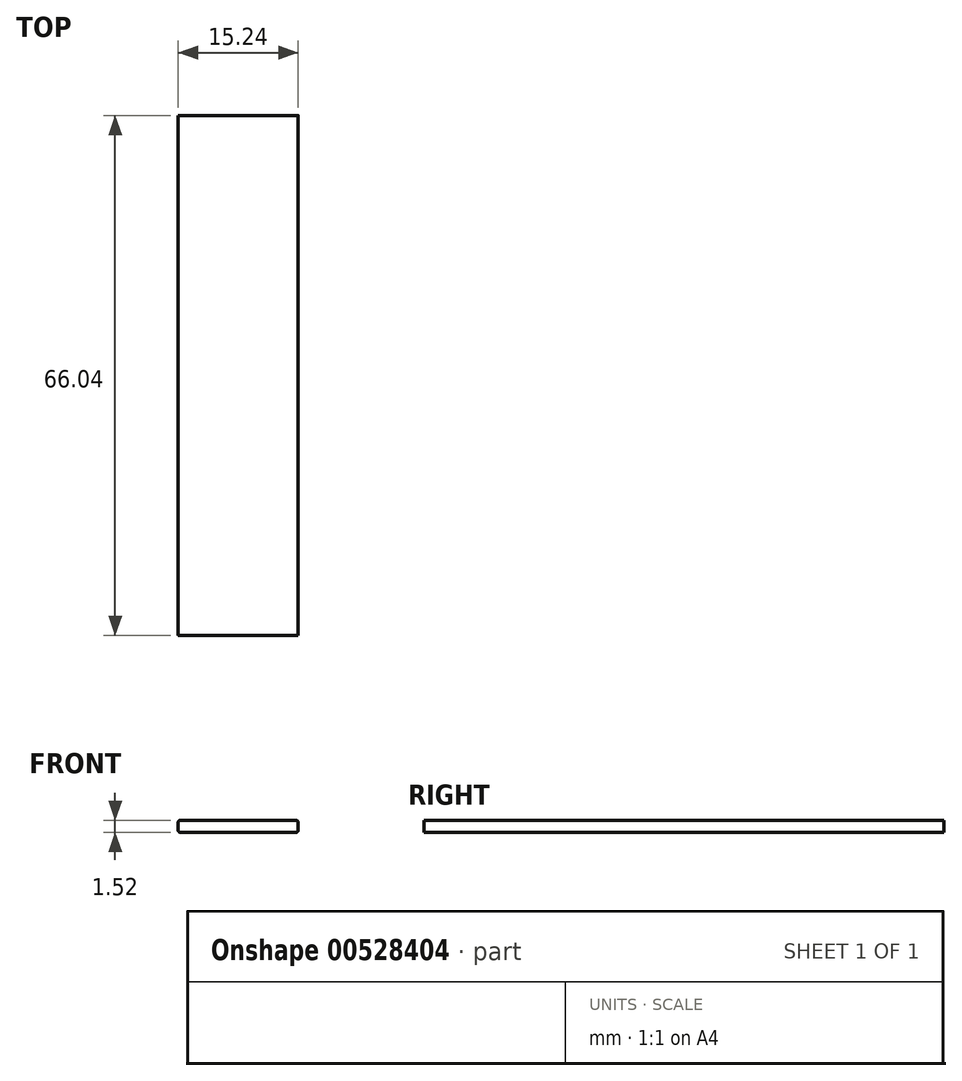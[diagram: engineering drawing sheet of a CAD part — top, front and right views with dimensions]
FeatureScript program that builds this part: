
annotation { "Feature Type Name" : "Feature", "Feature Type Description" : "" }
export const myFeature = defineFeature(function(context is Context, id is Id, definition is map)
    precondition{}
    {
        {
            var Q0;
            Q0=qCreatedBy(makeId("Front.planeOp"),FACE);
            var sketch = newSketch(context, id + "F0", { "sketchPlane" : qUnion([Q0])});
            skPoint(sketch, "E0.middle", {"position": v(0, 0) * mm});
            skLineSegment(sketch, "E1", {"start": v(-7.62, 3.62) * mm, "end": v(-7.62, 2.6) * mm});
            skPoint(sketch, "E2.visualSharp", {"position": v(-7.62, 2.35) * mm});
            skArc(sketch, "E2.filletArc", {"start": v(-7.62, 2.6) * mm, "mid": v(-7.55, 2.42) * mm, "end": v(-7.37, 2.35) * mm});
            skLineSegment(sketch, "E3", {"start": v(-7.37, 3.87) * mm, "end": v(0, 3.87) * mm});
            skPoint(sketch, "E4.visualSharp", {"position": v(-7.62, 3.87) * mm});
            skArc(sketch, "E4.filletArc", {"start": v(-7.37, 3.87) * mm, "mid": v(-7.55, 3.8) * mm, "end": v(-7.62, 3.62) * mm});
            skLineSegment(sketch, "E5", {"start": v(-7.37, 2.35) * mm, "end": v(0, 2.35) * mm});
            skLineSegment(sketch, "E6.MirrorCS", {"start": v(7.37, 3.87) * mm, "end": v(0, 3.87) * mm});
            skLineSegment(sketch, "E7.MirrorCS", {"start": v(7.62, 3.62) * mm, "end": v(7.62, 2.6) * mm});
            skLineSegment(sketch, "E8.MirrorCS", {"start": v(7.37, 2.35) * mm, "end": v(0, 2.35) * mm});
            skArc(sketch, "E9.MirrorCS", {"start": v(7.37, 3.87) * mm, "mid": v(7.55, 3.8) * mm, "end": v(7.62, 3.62) * mm});
            skArc(sketch, "E10.MirrorCS", {"start": v(7.62, 2.6) * mm, "mid": v(7.55, 2.42) * mm, "end": v(7.37, 2.35) * mm});
            skSolve(sketch);
        }
        {
            var Q0;
            Q0 = qSketchRegion(id + "F0", true);
            extrude(context, id + "F1", {"entities" : qUnion([Q0]), "depth" : 66.04 * mm, "offsetDistance" : 25.4 * mm});
        }
    });
